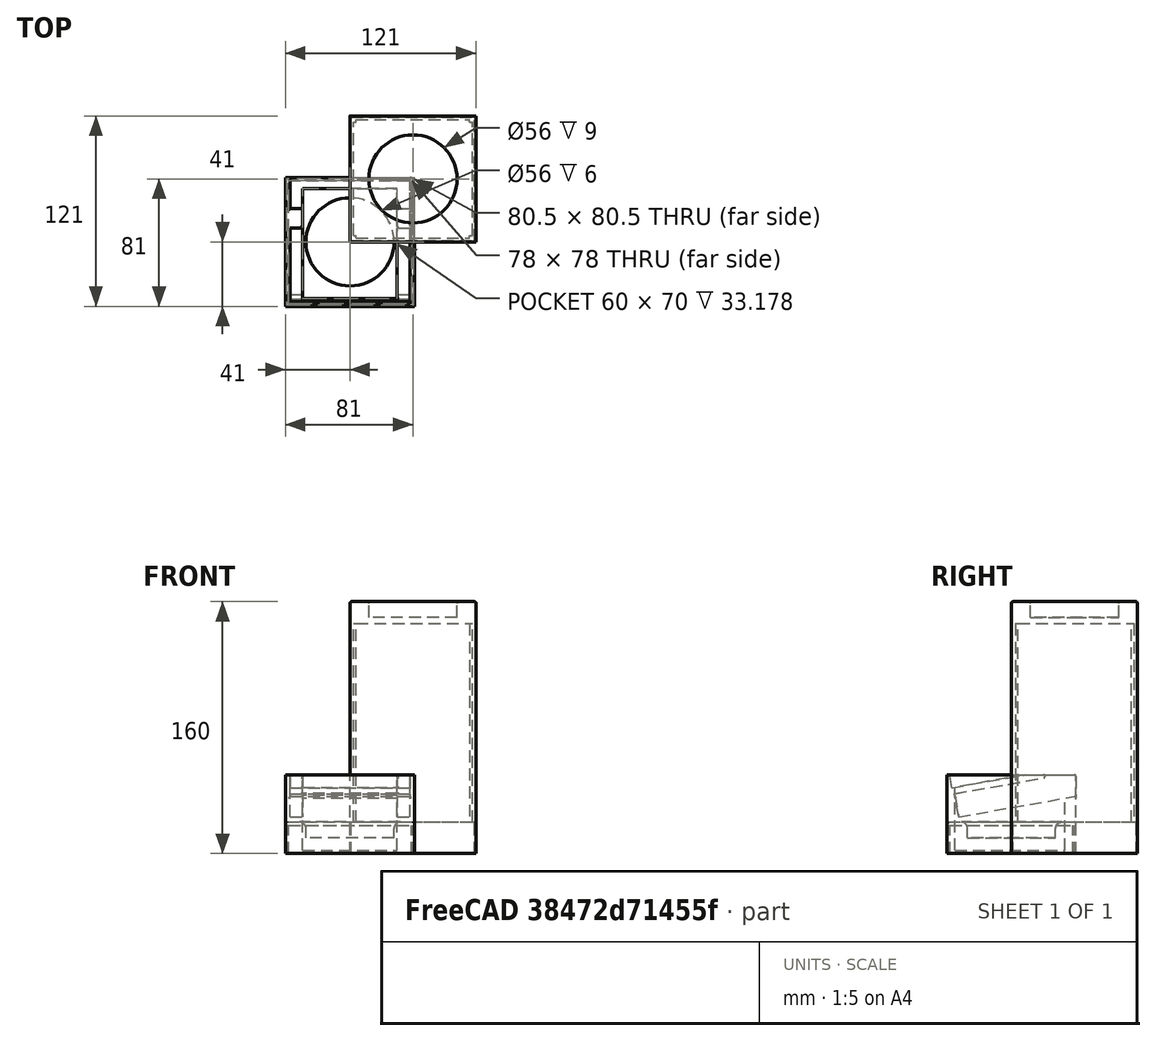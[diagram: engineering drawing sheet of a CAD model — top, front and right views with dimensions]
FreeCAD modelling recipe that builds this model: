
FCSTD DOCUMENT  (FreeCAD 0.19R24291 (Git))
Label: detska_kamera
License: All rights reserved
LicenseURL: http://en.wikipedia.org/wiki/All_rights_reserved
objects: Part::Box×16, Part::Cut×5, Part::MultiFuse×5, Part::Fillet×3, Part::Cylinder×2
note: 31 computed .brp shape members not serialized (recipe doc carries the construction recipe); baked Part::Feature solids carry a one-line shape summary decoded from their .brp

FEATURE [Part::Box] Box  label="Cube"
  AttacherType = Attacher::AttachEngine3D
  Height = 20
  Length = 82
  Placement = pos=(-41,-41,0) rot=(0,0,1;0rad)
  Width = 82
FEATURE [Part::Cylinder] Cylinder
  Angle = 360
  AttacherType = Attacher::AttachEngine3D
  Height = 10
  Placement = pos=(0,0,10) rot=(0,0,1;0rad)
  Radius = 28
FEATURE [Part::Box] Box003  label="Cube003"
  AttacherType = Attacher::AttachEngine3D
  Height = 18
  Length = 78
  Placement = pos=(-39,-39,0) rot=(0,0,1;0rad)
  Width = 78
FEATURE [Part::Box] Box004  label="Cube004"
  AttacherType = Attacher::AttachEngine3D
  Height = 18
  Length = 80.5
  Placement = pos=(-40.25,-40.25,0) rot=(0,0,1;0rad)
  Width = 80.5
FEATURE [Part::Cut] Cut
  Base = -> Box
  Tool = -> Box004
FEATURE [Part::MultiFuse] Fusion
  Shapes = -> [Cut,Box003]
FEATURE [Part::Cut] Cut001
  Base = -> Fusion
  Tool = -> Cylinder
FEATURE [Part::Fillet] Fillet  label="Fillet_kruh"
  Base = -> Cut001
  Edges = 5 edges: [Edge2 r=1,Edge7 r=1,Edge8 r=1,Edge9 r=1,Edge10 r=4]
FEATURE [Part::Box] Box005  label="Cube005_noha"
  AttacherType = Attacher::AttachEngine3D
  Height = 160
  Length = 80
  Width = 80
FEATURE [Part::Box] Box007  label="Cube006"
  AttacherType = Attacher::AttachEngine3D
  Height = 50
  Length = 82
  Placement = pos=(-41,-41,0) rot=(0,0,1;0rad)
  Width = 82
FEATURE [Part::Box] Box008  label="Cube007"
  AttacherType = Attacher::AttachEngine3D
  Height = 18
  Length = 78
  Placement = pos=(-39,-39,0) rot=(0,0,1;0rad)
  Width = 78
FEATURE [Part::Box] Box009  label="Cube008"
  AttacherType = Attacher::AttachEngine3D
  Height = 18
  Length = 80.5
  Placement = pos=(-40.25,-40.25,0) rot=(0,0,1;0rad)
  Width = 80.5
FEATURE [Part::Cut] Cut002
  Base = -> Box007
  Tool = -> Box009
FEATURE [Part::MultiFuse] Fusion001
  Shapes = -> [Cut002,Box008]
FEATURE [Part::Box] Box010  label="Cube009"
  AttacherType = Attacher::AttachEngine3D
  Height = 15
  Length = 76
  Placement = pos=(-38,-33.5854,23.2611) rot=(1,0,0;0.174533rad)
  Width = 90
FEATURE [Part::Box] Box011  label="Cube010"
  AttacherType = Attacher::AttachEngine3D
  Height = 90
  Length = 60
  Placement = pos=(-30,-36,2) rot=(0,0,1;0rad)
  Width = 70
FEATURE [Part::Box] Box012  label="Cube011"
  AttacherType = Attacher::AttachEngine3D
  Height = 15
  Length = 76
  Placement = pos=(-38,-37.8695,41.7988) rot=(1,0,0;0.174533rad)
  Width = 90
FEATURE [Part::MultiFuse] Fusion002
  Shapes = -> [Box010,Box011,Box012]
FEATURE [Part::Cut] Cut003
  Base = -> Fusion001
  Tool = -> Fusion002
FEATURE [Part::Fillet] Fillet001  label="Fillet001_stvorec"
  Base = -> Cut003
  Edges = 13 edges r=1: [Edge8,Edge9,Edge10,Edge18,Edge19,Edge20,Edge23,Edge24,Edge25,Edge35,Edge37,Edge41,Edge44]
FEATURE [Part::Box] Box013  label="Cube005_noha_up"
  AttacherType = Attacher::AttachEngine3D
  Height = 20
  Length = 78.5
  Placement = pos=(0.75,0.75,0) rot=(0,0,1;0rad)
  Width = 78.5
FEATURE [Part::Box] Box014  label="Cube005_nohaupup"
  AttacherType = Attacher::AttachEngine3D
  Height = 126
  Length = 75.4
  Placement = pos=(2.3,2.3,20) rot=(0,0,1;0rad)
  Width = 75.4
FEATURE [Part::Cylinder] Cylinder001
  Angle = 360
  AttacherType = Attacher::AttachEngine3D
  Height = 10
  Placement = pos=(40,40,150) rot=(0,0,1;0rad)
  Radius = 28
FEATURE [Part::MultiFuse] Fusion003
  Shapes = -> [Box014,Box013,Cylinder001]
FEATURE [Part::Cut] Cut004  label="Cut004_noha"
  Base = -> Box005
  Tool = -> Fusion003
FEATURE [Part::Fillet] Fillet002
  Base = -> Cut004
  Edges = 5 edges r=1: [Edge2,Edge7,Edge8,Edge9,Edge10]
FEATURE [Part::Box] Box016  label="Cube005_nohaupup001"
  AttacherType = Attacher::AttachEngine3D
  Height = 126
  Length = 3
  Placement = pos=(1,1,20) rot=(0,0,1;0rad)
  Width = 3
FEATURE [Part::Box] Box017  label="Cube005_nohaupup002"
  AttacherType = Attacher::AttachEngine3D
  Height = 126
  Length = 3
  Placement = pos=(1,76,20) rot=(0,0,1;0rad)
  Width = 3
FEATURE [Part::Box] Box018  label="Cube005_nohaupup003"
  AttacherType = Attacher::AttachEngine3D
  Height = 126
  Length = 3
  Placement = pos=(76,1,20) rot=(0,0,1;0rad)
  Width = 3
FEATURE [Part::Box] Box019  label="Cube005_nohaupup004"
  AttacherType = Attacher::AttachEngine3D
  Height = 126
  Length = 3
  Placement = pos=(76,76,20) rot=(0,0,1;0rad)
  Width = 3
FEATURE [Part::MultiFuse] Fusion004  label="Fusion004_noha"
  Shapes = -> [Fillet002,Box016,Box017,Box018,Box019]
